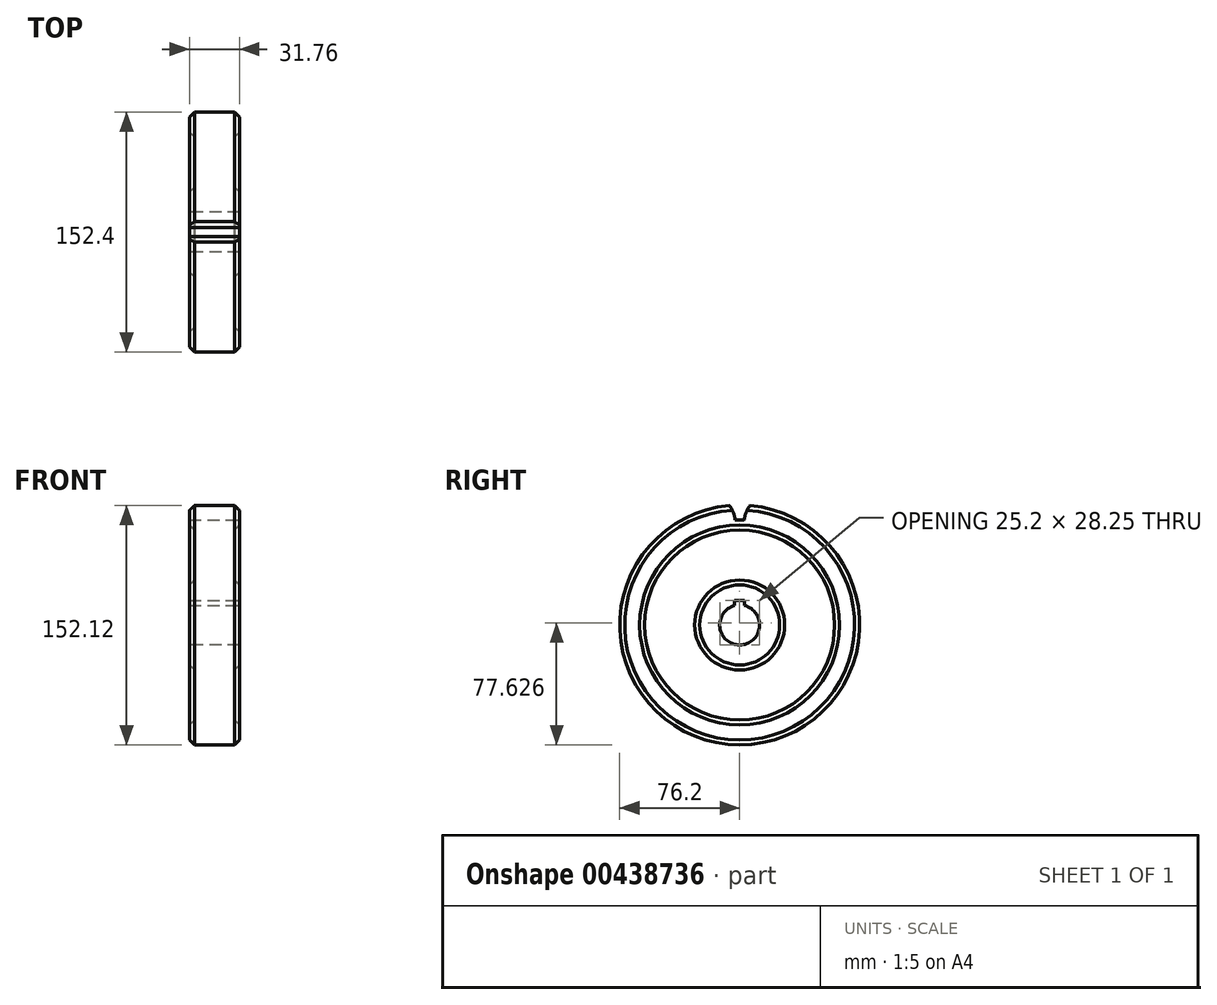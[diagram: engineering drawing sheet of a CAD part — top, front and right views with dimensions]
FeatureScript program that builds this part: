
annotation { "Feature Type Name" : "Feature", "Feature Type Description" : "" }
export const myFeature = defineFeature(function(context is Context, id is Id, definition is map)
    precondition{}
    {
        {
            var Q0;
            Q0=qCreatedBy(makeId("Front.planeOp"),FACE);
            var sketch = newSketch(context, id + "F0", { "sketchPlane" : qUnion([Q0])});
            skLineSegment(sketch, "E0", {"start": v(0, -18.57) * mm, "end": v(0, 44.93) * mm});
            skLineSegment(sketch, "E1", {"start": v(0, 44.93) * mm, "end": v(12.7, 44.93) * mm});
            skLineSegment(sketch, "E2", {"start": v(12.7, 44.93) * mm, "end": v(15.87, 41.75) * mm});
            skLineSegment(sketch, "E3", {"start": v(15.87, 41.75) * mm, "end": v(15.87, 32.23) * mm});
            skLineSegment(sketch, "E4", {"start": v(15.88, 32.23) * mm, "end": v(12.7, 29.05) * mm});
            skLineSegment(sketch, "E5", {"start": v(12.7, 29.05) * mm, "end": v(12.7, -2.7) * mm});
            skLineSegment(sketch, "E6", {"start": v(12.7, -2.7) * mm, "end": v(15.88, -5.87) * mm});
            skLineSegment(sketch, "E7", {"start": v(15.88, -5.87) * mm, "end": v(15.88, -18.57) * mm});
            skLineSegment(sketch, "E8", {"start": v(15.88, -18.57) * mm, "end": v(0, -18.57) * mm});
            skLineSegment(sketch, "E9", {"start": v(0, -18.57) * mm, "end": v(0, -31.27) * mm});
            skLineSegment(sketch, "E10", {"start": v(0, -31.27) * mm, "end": v(5.54, -31.27) * mm});
            skLineSegment(sketch, "E11.MirrorCS", {"start": v(0, 44.93) * mm, "end": v(-12.7, 44.93) * mm});
            skLineSegment(sketch, "E12.MirrorCS", {"start": v(-12.7, 44.93) * mm, "end": v(-15.88, 41.75) * mm});
            skLineSegment(sketch, "E13.MirrorCS", {"start": v(-15.88, 41.75) * mm, "end": v(-15.88, 32.23) * mm});
            skLineSegment(sketch, "E14.MirrorCS", {"start": v(-12.7, 29.05) * mm, "end": v(-12.7, -2.7) * mm});
            skLineSegment(sketch, "E15.MirrorCS", {"start": v(-15.88, 32.23) * mm, "end": v(-12.7, 29.05) * mm});
            skLineSegment(sketch, "E16.MirrorCS", {"start": v(-12.7, -2.7) * mm, "end": v(-15.88, -5.87) * mm});
            skLineSegment(sketch, "E17.MirrorCS", {"start": v(-15.88, -5.87) * mm, "end": v(-15.88, -18.57) * mm});
            skLineSegment(sketch, "E18.MirrorCS", {"start": v(-15.88, -18.57) * mm, "end": v(0, -18.57) * mm});
            skSolve(sketch);
        }
        {
            var Q0;
            Q0=makeQuery(id+"F0.imprint","IMPRINT",FACE,{"disambiguationData":[TD([[makeQuery(id+"F0.imprint","IMPRINT",EDGE,{"derivedFrom":sQuery(id+"F0.wireOp",EDGE,"E0")}),-1.0]])]});
            var Q1;
            Q1=makeQuery(id+"F0.imprint","IMPRINT",FACE,{"disambiguationData":[TD([[makeQuery(id+"F0.imprint","IMPRINT",EDGE,{"derivedFrom":sQuery(id+"F0.wireOp",EDGE,"E0")}),1.0]])]});
            var Q2;
            Q2=sQuery(id+"F0.wireOp",EDGE,"E10");
            revolve(context, id + "F1", {"entities" : qUnion([Q0, Q1]), "axis" : qUnion([Q2]), "revolveType" : RevolveType.FULL});
        }
        {
            var Q0;
            Q0=makeQuery(id+"F1.opRevolve","SWEPT_FACE",FACE,{"disambiguationData":[OSD([sQuery(id+"F0.wireOp",EDGE,"E3")])]});
            var sketch = newSketch(context, id + "F2", { "sketchPlane" : qUnion([Q0])});
            skLineSegment(sketch, "E19", {"start": v(0, -31.27) * mm, "end": v(0, 77.49) * mm});
            skLineSegment(sketch, "E20", {"start": v(0, 35.4) * mm, "end": v(2.86, 35.4) * mm});
            skArc(sketch, "E21", {"start": v(6.54, 44.65) * mm, "mid": v(4.08, 40.27) * mm, "end": v(2.86, 35.4) * mm});
            skCircle(sketch, "E22.0", {"center": v(0, -31.27) * mm, "radius": 76.2 * mm});
            skLineSegment(sketch, "E23.MirrorCS", {"start": v(0, 35.4) * mm, "end": v(-2.86, 35.4) * mm});
            skArc(sketch, "E24.MirrorCS", {"start": v(-6.54, 44.65) * mm, "mid": v(-4.08, 40.27) * mm, "end": v(-2.86, 35.4) * mm});
            skSolve(sketch);
        }
        {
            var Q0;
            {var subQ0=sQuery(id+"F2.wireOp",EDGE,"E22.0");var subQ5=sQuery(id+"F2.wireOp",EDGE,"E24.MirrorCS");var subQ6=makeQuery(id+"F2.imprint","INTERSECT",VERTEX,{"derivedFrom":[subQ0,subQ5]});Q0=makeQuery(id+"F2.imprint","IMPRINT",FACE,{"disambiguationData":[TD([[makeQuery(id+"F2.imprint","IMPRINT",EDGE,{"disambiguationData":[TD([[subQ6,1.0]])],"derivedFrom":subQ0}),1.0]])]});}
            var Q1;
            {var subQ0=sQuery(id+"F2.wireOp",EDGE,"E23.MirrorCS");Q1=makeQuery(id+"F2.imprint","IMPRINT",FACE,{"disambiguationData":[TD([[makeQuery(id+"F2.imprint","IMPRINT",EDGE,{"derivedFrom":subQ0}),-1.0]])]});}
            var Q2;
            {var subQ0=sQuery(id+"F2.wireOp",EDGE,"E20");Q2=makeQuery(id+"F2.imprint","IMPRINT",FACE,{"disambiguationData":[TD([[makeQuery(id+"F2.imprint","IMPRINT",EDGE,{"derivedFrom":subQ0}),1.0]])]});}
            var Q3;
            {var subQ0=sQuery(id+"F2.wireOp",EDGE,"E22.0");var subQ5=sQuery(id+"F2.wireOp",EDGE,"E21");var subQ6=makeQuery(id+"F2.imprint","INTERSECT",VERTEX,{"derivedFrom":[subQ5,subQ0]});Q3=makeQuery(id+"F2.imprint","IMPRINT",FACE,{"disambiguationData":[TD([[makeQuery(id+"F2.imprint","IMPRINT",EDGE,{"disambiguationData":[TD([[subQ6,-1.0]])],"derivedFrom":subQ0}),1.0]])]});}
            extrude(context, id + "F3", {"entities" : qUnion([Q0, Q1, Q2, Q3]), "operationType" : NewBodyOperationType.REMOVE, "endBound" : BoundingType.THROUGH_ALL, "oppositeDirection" : true, "depth" : 25.4 * mm});
        }
        {
            var Q0;
            Q0=makeQuery(id+"F1.opRevolve","SWEPT_FACE",FACE,{"disambiguationData":[OSD([sQuery(id+"F0.wireOp",EDGE,"E7")])]});
            var sketch = newSketch(context, id + "F4", { "sketchPlane" : qUnion([Q0])});
            skLineSegment(sketch, "E25", {"start": v(0, -31.27) * mm, "end": v(0, 61.87) * mm});
            skLineSegment(sketch, "E26", {"start": v(0, -15.72) * mm, "end": v(3.18, -15.72) * mm});
            skLineSegment(sketch, "E27", {"start": v(3.17, -15.72) * mm, "end": v(3.17, -18.97) * mm});
            skArc(sketch, "E28.0", {"start": v(3.18, -18.97) * mm, "mid": v(0, -18.57) * mm, "end": v(-3.17, -18.97) * mm});
            skLineSegment(sketch, "E29.MirrorCS", {"start": v(0, -15.72) * mm, "end": v(-3.18, -15.72) * mm});
            skLineSegment(sketch, "E30.MirrorCS", {"start": v(-3.18, -15.72) * mm, "end": v(-3.17, -18.97) * mm});
            skSolve(sketch);
        }
        {
            var Q0;
            {var subQ0=sQuery(id+"F4.wireOp",EDGE,"E29.MirrorCS");Q0=makeQuery(id+"F4.imprint","IMPRINT",FACE,{"disambiguationData":[TD([[makeQuery(id+"F4.imprint","IMPRINT",EDGE,{"derivedFrom":subQ0}),1.0]])]});}
            var Q1;
            {var subQ0=sQuery(id+"F4.wireOp",EDGE,"E26");Q1=makeQuery(id+"F4.imprint","IMPRINT",FACE,{"disambiguationData":[TD([[makeQuery(id+"F4.imprint","IMPRINT",EDGE,{"derivedFrom":subQ0}),-1.0]])]});}
            extrude(context, id + "F5", {"entities" : qUnion([Q0, Q1]), "operationType" : NewBodyOperationType.REMOVE, "endBound" : BoundingType.THROUGH_ALL, "oppositeDirection" : true, "depth" : 25.4 * mm});
        }
    });
